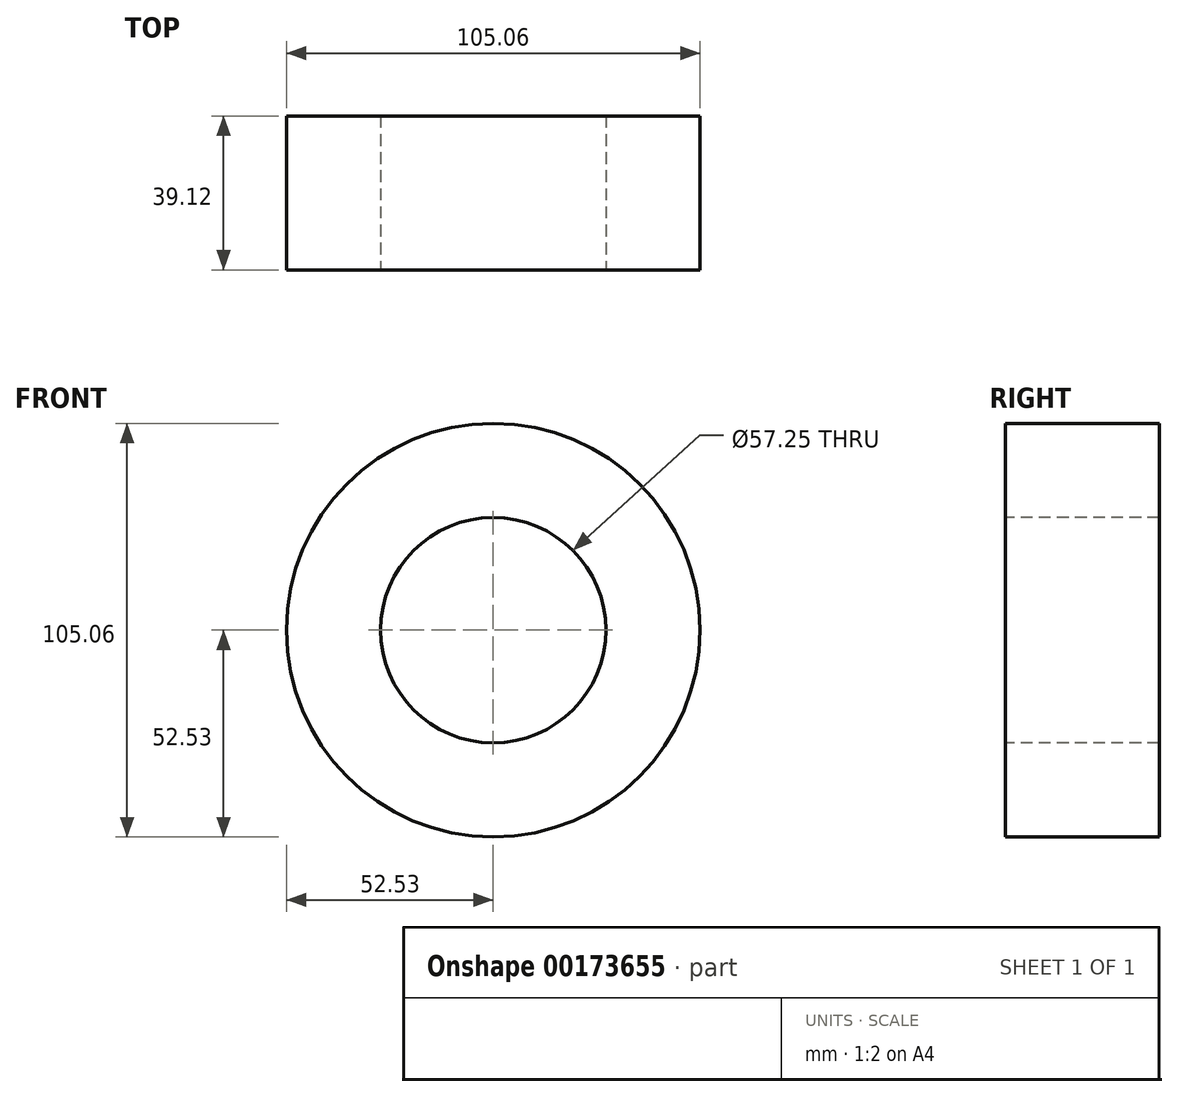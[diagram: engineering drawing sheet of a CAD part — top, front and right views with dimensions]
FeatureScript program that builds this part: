
annotation { "Feature Type Name" : "Feature", "Feature Type Description" : "" }
export const myFeature = defineFeature(function(context is Context, id is Id, definition is map)
    precondition{}
    {
        {
            var Q0;
            Q0=qCreatedBy(makeId("Front.planeOp"),FACE);
            var sketch = newSketch(context, id + "F0", { "sketchPlane" : qUnion([Q0])});
            skCircle(sketch, "E0", {"center": v(0, 0) * mm, "radius": 52.53 * mm});
            skCircle(sketch, "E1", {"center": v(0, 0) * mm, "radius": 28.63 * mm});
            skCircle(sketch, "E2", {"center": v(0, 0) * mm, "radius": 13.7 * mm});
            skSolve(sketch);
        }
        {
            var Q0;
            Q0=makeQuery(id+"F0.imprint","IMPRINT",FACE,{"disambiguationData":[TD([[makeQuery(id+"F0.imprint","IMPRINT",EDGE,{"derivedFrom":sQuery(id+"F0.wireOp",EDGE,"E0")}),1.0]])]});
            extrude(context, id + "F1", {"entities" : qUnion([Q0]), "oppositeDirection" : true, "depth" : 39.12 * mm});
        }
    });
